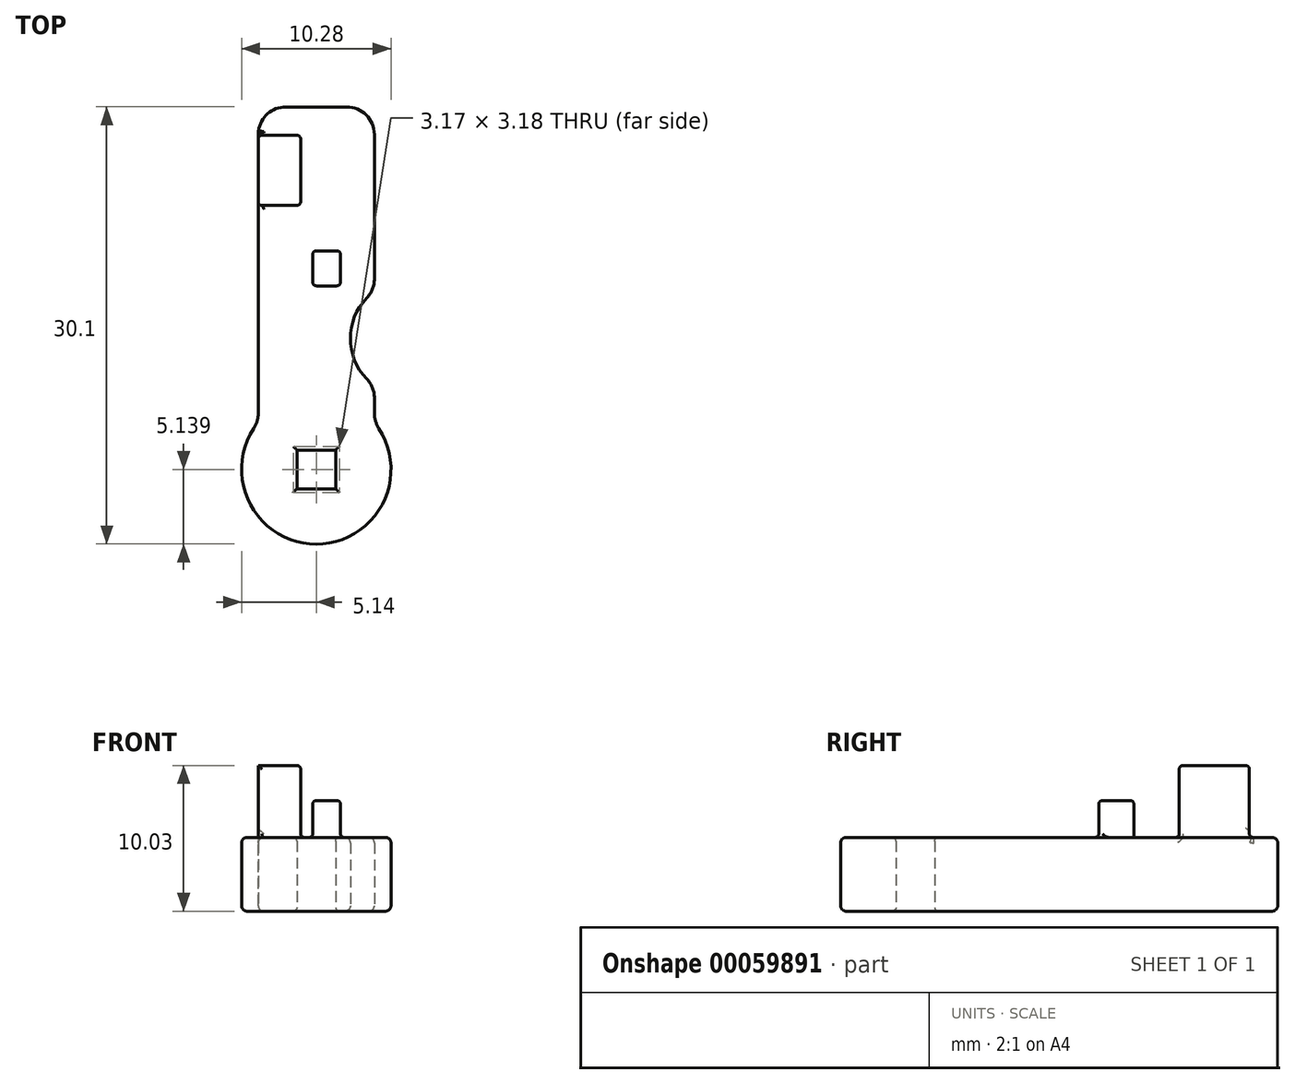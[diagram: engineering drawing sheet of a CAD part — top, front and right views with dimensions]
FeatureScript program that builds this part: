
annotation { "Feature Type Name" : "Feature", "Feature Type Description" : "" }
export const myFeature = defineFeature(function(context is Context, id is Id, definition is map)
    precondition{}
    {
        {
            var Q0;
            Q0=qCreatedBy(makeId("Top.planeOp"),FACE);
            var sketch = newSketch(context, id + "F0", { "sketchPlane" : qUnion([Q0])});
            skLineSegment(sketch, "E0.rect.bottom", {"start": v(4, 14.6) * mm, "end": v(-4, 14.6) * mm});
            skLineSegment(sketch, "E0.rect.left", {"start": v(4, 14.6) * mm, "end": v(4, 1.9) * mm});
            skLineSegment(sketch, "E0.rect.right", {"start": v(-4, 14.6) * mm, "end": v(-4, -7.12) * mm});
            skPoint(sketch, "E0.rect.middle", {"position": v(0, 0) * mm});
            skLineSegment(sketch, "E1.rect.bottom", {"start": v(1.33, -9.02) * mm, "end": v(-1.33, -9.02) * mm});
            skLineSegment(sketch, "E1.rect.top", {"start": v(1.33, -11.68) * mm, "end": v(-1.33, -11.68) * mm});
            skLineSegment(sketch, "E1.rect.left", {"start": v(1.33, -9.02) * mm, "end": v(1.33, -11.68) * mm});
            skLineSegment(sketch, "E1.rect.right", {"start": v(-1.33, -9.02) * mm, "end": v(-1.33, -11.68) * mm});
            skPoint(sketch, "E1.rect.middle", {"position": v(0, -10.35) * mm});
            skCircle(sketch, "E2", {"center": v(0, -10.35) * mm, "radius": 5.14 * mm});
            skArc(sketch, "E3", {"start": v(4, 1.9) * mm, "mid": v(2.35, -1.34) * mm, "end": v(4, -4.58) * mm});
            skLineSegment(sketch, "E4.trimOffspring", {"start": v(4, -4.58) * mm, "end": v(4, -7.12) * mm});
            skPoint(sketch, "E5.orphan", {"position": v(4, -14.6) * mm});
            skPoint(sketch, "E6.orphan", {"position": v(-4, -14.6) * mm});
            skLineSegment(sketch, "E7.rect.bottom", {"start": v(1.66, 2.29) * mm, "end": v(-0.24, 2.29) * mm});
            skLineSegment(sketch, "E7.rect.top", {"start": v(1.66, 4.7) * mm, "end": v(-0.24, 4.7) * mm});
            skLineSegment(sketch, "E7.rect.left", {"start": v(1.66, 2.29) * mm, "end": v(1.66, 4.7) * mm});
            skLineSegment(sketch, "E7.rect.right", {"start": v(-0.24, 2.29) * mm, "end": v(-0.24, 4.7) * mm});
            skPoint(sketch, "E7.rect.middle", {"position": v(0.71, 3.5) * mm});
            skLineSegment(sketch, "E8.bottom", {"start": v(-4, 12.65) * mm, "end": v(-1.08, 12.65) * mm});
            skLineSegment(sketch, "E8.top", {"start": v(-4, 7.82) * mm, "end": v(-1.08, 7.82) * mm});
            skLineSegment(sketch, "E8.left", {"start": v(-4, 12.65) * mm, "end": v(-4, 7.82) * mm});
            skLineSegment(sketch, "E8.right", {"start": v(-1.08, 12.65) * mm, "end": v(-1.08, 7.82) * mm});
            skSolve(sketch);
        }
        {
            var Q0;
            Q0 = qSketchRegion(id + "F0", true);
            var Q1;
            Q1=makeQuery(id+"F0.imprint","IMPRINT",FACE,{"disambiguationData":[TD([[makeQuery(id+"F0.imprint","IMPRINT",EDGE,{"derivedFrom":sQuery(id+"F0.wireOp",EDGE,"E7.rect.bottom")}),-1.0]])]});
            extrude(context, id + "F1", {"entities" : qUnion([Q0, Q1]), "depth" : 5.08 * mm});
        }
        {
            var Q0;
            Q0=makeQuery(id+"F0.imprint","IMPRINT",FACE,{"disambiguationData":[TD([[makeQuery(id+"F0.imprint","IMPRINT",EDGE,{"derivedFrom":sQuery(id+"F0.wireOp",EDGE,"E8.bottom")}),-1.0]])]});
            extrude(context, id + "F2", {"entities" : qUnion([Q0]), "operationType" : NewBodyOperationType.ADD, "depth" : 10.03 * mm});
        }
        {
            var Q0;
            Q0=makeQuery(id+"F0.imprint","IMPRINT",FACE,{"disambiguationData":[TD([[makeQuery(id+"F0.imprint","IMPRINT",EDGE,{"derivedFrom":sQuery(id+"F0.wireOp",EDGE,"E7.rect.bottom")}),-1.0]])]});
            extrude(context, id + "F3", {"entities" : qUnion([Q0]), "operationType" : NewBodyOperationType.ADD, "depth" : 7.62 * mm});
        }
        {
            var Q0;
            Q0=makeQuery(id+"F1.opExtrude","SWEPT_EDGE",EDGE,{"disambiguationData":[OSD([sQuery(id+"F0.wireOp",EDGE,"E0.rect.left"),sQuery(id+"F0.wireOp",EDGE,"E3")])]});
            var Q1;
            Q1=makeQuery(id+"F1.opExtrude","SWEPT_EDGE",EDGE,{"disambiguationData":[OSD([sQuery(id+"F0.wireOp",EDGE,"E3"),sQuery(id+"F0.wireOp",EDGE,"E4.trimOffspring")])]});
            var Q2;
            Q2=makeQuery(id+"F1.opExtrude","SWEPT_EDGE",EDGE,{"disambiguationData":[OSD([sQuery(id+"F0.wireOp",EDGE,"E2"),sQuery(id+"F0.wireOp",EDGE,"E4.trimOffspring")])]});
            var Q3;
            Q3=makeQuery(id+"F1.opExtrude","SWEPT_EDGE",EDGE,{"disambiguationData":[OSD([sQuery(id+"F0.wireOp",EDGE,"E0.rect.right"),sQuery(id+"F0.wireOp",EDGE,"E2")])]});
            var Q4;
            Q4=makeQuery(id+"F1.opExtrude","SWEPT_EDGE",EDGE,{"disambiguationData":[OSD([sQuery(id+"F0.wireOp",EDGE,"E0.rect.bottom"),sQuery(id+"F0.wireOp",EDGE,"E0.rect.right")])]});
            var Q5;
            Q5=makeQuery(id+"F1.opExtrude","SWEPT_EDGE",EDGE,{"disambiguationData":[OSD([sQuery(id+"F0.wireOp",EDGE,"E0.rect.bottom"),sQuery(id+"F0.wireOp",EDGE,"E0.rect.left")])]});
            fillet(context, id + "F4", {"entities" : qUnion([Q0, Q1, Q2, Q3, Q4, Q5]), "radius" : 1.9 * mm, "tangentPropagation" : true, "allowEdgeOverflow" : false});
        }
        {
            var Q0;
            Q0=makeQuery(id+"F2.opExtrude","CAP_EDGE",EDGE,{"disambiguationData":[OSD([sQuery(id+"F0.wireOp",EDGE,"E8.right")])],"isStart":false});
            var Q1;
            Q1=makeQuery(id+"F2.opExtrude","CAP_EDGE",EDGE,{"disambiguationData":[OSD([sQuery(id+"F0.wireOp",EDGE,"E8.top")])],"isStart":false});
            var Q2;
            Q2=makeQuery(id+"F2.opExtrude","CAP_EDGE",EDGE,{"disambiguationData":[OSD([sQuery(id+"F0.wireOp",EDGE,"E8.left")])],"isStart":false});
            var Q3;
            Q3=makeQuery(id+"F2.opExtrude","CAP_EDGE",EDGE,{"disambiguationData":[OSD([sQuery(id+"F0.wireOp",EDGE,"E8.bottom")])],"isStart":false});
            var Q4;
            Q4=makeQuery(id+"F2.opExtrude","SWEPT_EDGE",EDGE,{"disambiguationData":[OSD([sQuery(id+"F0.wireOp",EDGE,"E8.top"),sQuery(id+"F0.wireOp",EDGE,"E8.right")])]});
            var Q5;
            Q5=makeQuery(id+"F2.opExtrude","SWEPT_EDGE",EDGE,{"disambiguationData":[OSD([sQuery(id+"F0.wireOp",EDGE,"E0.rect.right"),sQuery(id+"F0.wireOp",EDGE,"E8.top"),sQuery(id+"F0.wireOp",EDGE,"E8.left")])]});
            var Q6;
            Q6=makeQuery(id+"F2.opExtrude","SWEPT_EDGE",EDGE,{"disambiguationData":[OSD([sQuery(id+"F0.wireOp",EDGE,"E8.bottom"),sQuery(id+"F0.wireOp",EDGE,"E8.right")])]});
            var Q7;
            Q7=makeQuery(id+"F2.opExtrude","SWEPT_EDGE",EDGE,{"disambiguationData":[OSD([sQuery(id+"F0.wireOp",EDGE,"E0.rect.right"),sQuery(id+"F0.wireOp",EDGE,"E8.bottom"),sQuery(id+"F0.wireOp",EDGE,"E8.left")])]});
            var Q8;
            Q8=makeQuery(id+"F3.opExtrude","SWEPT_EDGE",EDGE,{"disambiguationData":[OSD([sQuery(id+"F0.wireOp",EDGE,"E7.rect.bottom"),sQuery(id+"F0.wireOp",EDGE,"E7.rect.right")])]});
            var Q9;
            Q9=makeQuery(id+"F3.opExtrude","CAP_EDGE",EDGE,{"disambiguationData":[OSD([sQuery(id+"F0.wireOp",EDGE,"E7.rect.right")])],"isStart":false});
            var Q10;
            Q10=makeQuery(id+"F3.opExtrude","CAP_EDGE",EDGE,{"disambiguationData":[OSD([sQuery(id+"F0.wireOp",EDGE,"E7.rect.bottom")])],"isStart":false});
            var Q11;
            Q11=makeQuery(id+"F3.opExtrude","SWEPT_EDGE",EDGE,{"disambiguationData":[OSD([sQuery(id+"F0.wireOp",EDGE,"E7.rect.bottom"),sQuery(id+"F0.wireOp",EDGE,"E7.rect.left")])]});
            var Q12;
            Q12=makeQuery(id+"F3.opExtrude","CAP_EDGE",EDGE,{"disambiguationData":[OSD([sQuery(id+"F0.wireOp",EDGE,"E7.rect.left")])],"isStart":false});
            var Q13;
            Q13=makeQuery(id+"F3.opExtrude","CAP_EDGE",EDGE,{"disambiguationData":[OSD([sQuery(id+"F0.wireOp",EDGE,"E7.rect.top")])],"isStart":false});
            var Q14;
            Q14=makeQuery(id+"F3.opExtrude","SWEPT_EDGE",EDGE,{"disambiguationData":[OSD([sQuery(id+"F0.wireOp",EDGE,"E7.rect.top"),sQuery(id+"F0.wireOp",EDGE,"E7.rect.left")])]});
            var Q15;
            Q15=makeQuery(id+"F3.opExtrude","SWEPT_EDGE",EDGE,{"disambiguationData":[OSD([sQuery(id+"F0.wireOp",EDGE,"E7.rect.top"),sQuery(id+"F0.wireOp",EDGE,"E7.rect.right")])]});
            var Q16;
            Q16=makeQuery(id+"F3.boolean.opBoolean","INTERSECT",EDGE,{"derivedFrom":[makeQuery(id+"F1.opExtrude","CAP_FACE",FACE,{"disambiguationData":[OSD([sQuery(id+"F0.wireOp",EDGE,"E0.rect.bottom"),sQuery(id+"F0.wireOp",EDGE,"E0.rect.left"),sQuery(id+"F0.wireOp",EDGE,"E0.rect.right"),sQuery(id+"F0.wireOp",EDGE,"E1.rect.bottom"),sQuery(id+"F0.wireOp",EDGE,"E1.rect.top"),sQuery(id+"F0.wireOp",EDGE,"E1.rect.left"),sQuery(id+"F0.wireOp",EDGE,"E1.rect.right"),sQuery(id+"F0.wireOp",EDGE,"E2"),sQuery(id+"F0.wireOp",EDGE,"E3"),sQuery(id+"F0.wireOp",EDGE,"E4.trimOffspring"),sQuery(id+"F0.wireOp",EDGE,"E8.left")])],"isStart":false}),makeQuery(id+"F3.opExtrude","SWEPT_FACE",FACE,{"disambiguationData":[OSD([sQuery(id+"F0.wireOp",EDGE,"E7.rect.bottom")])]})]});
            fillet(context, id + "F5", {"entities" : qUnion([Q0, Q1, Q2, Q3, Q4, Q5, Q6, Q7, Q8, Q9, Q10, Q11, Q12, Q13, Q14, Q15, Q16]), "radius" : 0.25 * mm, "tangentPropagation" : true, "allowEdgeOverflow" : false});
        }
        {
            var Q0;
            Q0=makeQuery(id+"F2.boolean.opBoolean","INTERSECT",EDGE,{"derivedFrom":[makeQuery(id+"F1.opExtrude","CAP_FACE",FACE,{"disambiguationData":[OSD([sQuery(id+"F0.wireOp",EDGE,"E0.rect.bottom"),sQuery(id+"F0.wireOp",EDGE,"E0.rect.left"),sQuery(id+"F0.wireOp",EDGE,"E0.rect.right"),sQuery(id+"F0.wireOp",EDGE,"E1.rect.bottom"),sQuery(id+"F0.wireOp",EDGE,"E1.rect.top"),sQuery(id+"F0.wireOp",EDGE,"E1.rect.left"),sQuery(id+"F0.wireOp",EDGE,"E1.rect.right"),sQuery(id+"F0.wireOp",EDGE,"E2"),sQuery(id+"F0.wireOp",EDGE,"E3"),sQuery(id+"F0.wireOp",EDGE,"E4.trimOffspring"),sQuery(id+"F0.wireOp",EDGE,"E8.left")])],"isStart":false}),makeQuery(id+"F2.opExtrude","SWEPT_FACE",FACE,{"disambiguationData":[OSD([sQuery(id+"F0.wireOp",EDGE,"E8.top")])]})]});
            var Q1;
            Q1=makeQuery(id+"F5.opFillet","BLEND_EDGE",EDGE,{"blendedFrom":[makeQuery(id+"F2.opExtrude","SWEPT_EDGE",EDGE,{"disambiguationData":[OSD([sQuery(id+"F0.wireOp",EDGE,"E8.top"),sQuery(id+"F0.wireOp",EDGE,"E8.right")])]}),makeQuery(id+"F1.opExtrude","CAP_FACE",FACE,{"disambiguationData":[OSD([sQuery(id+"F0.wireOp",EDGE,"E0.rect.bottom"),sQuery(id+"F0.wireOp",EDGE,"E0.rect.left"),sQuery(id+"F0.wireOp",EDGE,"E0.rect.right"),sQuery(id+"F0.wireOp",EDGE,"E1.rect.bottom"),sQuery(id+"F0.wireOp",EDGE,"E1.rect.top"),sQuery(id+"F0.wireOp",EDGE,"E1.rect.left"),sQuery(id+"F0.wireOp",EDGE,"E1.rect.right"),sQuery(id+"F0.wireOp",EDGE,"E2"),sQuery(id+"F0.wireOp",EDGE,"E3"),sQuery(id+"F0.wireOp",EDGE,"E4.trimOffspring"),sQuery(id+"F0.wireOp",EDGE,"E8.left")])],"isStart":false})],"blendedInto":[makeQuery(id+"F1.opExtrude","CAP_FACE",FACE,{"disambiguationData":[OSD([sQuery(id+"F0.wireOp",EDGE,"E0.rect.bottom"),sQuery(id+"F0.wireOp",EDGE,"E0.rect.left"),sQuery(id+"F0.wireOp",EDGE,"E0.rect.right"),sQuery(id+"F0.wireOp",EDGE,"E1.rect.bottom"),sQuery(id+"F0.wireOp",EDGE,"E1.rect.top"),sQuery(id+"F0.wireOp",EDGE,"E1.rect.left"),sQuery(id+"F0.wireOp",EDGE,"E1.rect.right"),sQuery(id+"F0.wireOp",EDGE,"E2"),sQuery(id+"F0.wireOp",EDGE,"E3"),sQuery(id+"F0.wireOp",EDGE,"E4.trimOffspring"),sQuery(id+"F0.wireOp",EDGE,"E8.left")])],"isStart":false})]});
            var Q2;
            {var subQ0=sQuery(id+"F0.wireOp",EDGE,"E8.left");var subQ1=sQuery(id+"F0.wireOp",EDGE,"E0.rect.right");Q2=makeQuery(id+"F5.opFillet","BLEND_EDGE",EDGE,{"blendedFrom":[makeQuery(id+"F2.opExtrude","SWEPT_EDGE",EDGE,{"disambiguationData":[OSD([subQ1,sQuery(id+"F0.wireOp",EDGE,"E8.top"),subQ0])]}),makeQuery(id+"F1.opExtrude","CAP_FACE",FACE,{"disambiguationData":[OSD([sQuery(id+"F0.wireOp",EDGE,"E0.rect.bottom"),sQuery(id+"F0.wireOp",EDGE,"E0.rect.left"),subQ1,sQuery(id+"F0.wireOp",EDGE,"E1.rect.bottom"),sQuery(id+"F0.wireOp",EDGE,"E1.rect.top"),sQuery(id+"F0.wireOp",EDGE,"E1.rect.left"),sQuery(id+"F0.wireOp",EDGE,"E1.rect.right"),sQuery(id+"F0.wireOp",EDGE,"E2"),sQuery(id+"F0.wireOp",EDGE,"E3"),sQuery(id+"F0.wireOp",EDGE,"E4.trimOffspring"),subQ0])],"isStart":false})],"blendedInto":[makeQuery(id+"F1.opExtrude","CAP_FACE",FACE,{"disambiguationData":[OSD([sQuery(id+"F0.wireOp",EDGE,"E0.rect.bottom"),sQuery(id+"F0.wireOp",EDGE,"E0.rect.left"),subQ1,sQuery(id+"F0.wireOp",EDGE,"E1.rect.bottom"),sQuery(id+"F0.wireOp",EDGE,"E1.rect.top"),sQuery(id+"F0.wireOp",EDGE,"E1.rect.left"),sQuery(id+"F0.wireOp",EDGE,"E1.rect.right"),sQuery(id+"F0.wireOp",EDGE,"E2"),sQuery(id+"F0.wireOp",EDGE,"E3"),sQuery(id+"F0.wireOp",EDGE,"E4.trimOffspring"),subQ0])],"isStart":false})]});}
            var Q3;
            Q3=makeQuery(id+"F2.boolean.opBoolean","INTERSECT",EDGE,{"derivedFrom":[makeQuery(id+"F1.opExtrude","CAP_FACE",FACE,{"disambiguationData":[OSD([sQuery(id+"F0.wireOp",EDGE,"E0.rect.bottom"),sQuery(id+"F0.wireOp",EDGE,"E0.rect.left"),sQuery(id+"F0.wireOp",EDGE,"E0.rect.right"),sQuery(id+"F0.wireOp",EDGE,"E1.rect.bottom"),sQuery(id+"F0.wireOp",EDGE,"E1.rect.top"),sQuery(id+"F0.wireOp",EDGE,"E1.rect.left"),sQuery(id+"F0.wireOp",EDGE,"E1.rect.right"),sQuery(id+"F0.wireOp",EDGE,"E2"),sQuery(id+"F0.wireOp",EDGE,"E3"),sQuery(id+"F0.wireOp",EDGE,"E4.trimOffspring"),sQuery(id+"F0.wireOp",EDGE,"E8.left")])],"isStart":false}),makeQuery(id+"F2.opExtrude","SWEPT_FACE",FACE,{"disambiguationData":[OSD([sQuery(id+"F0.wireOp",EDGE,"E8.right")])]})]});
            var Q4;
            Q4=makeQuery(id+"F5.opFillet","BLEND_EDGE",EDGE,{"blendedFrom":[makeQuery(id+"F2.opExtrude","SWEPT_EDGE",EDGE,{"disambiguationData":[OSD([sQuery(id+"F0.wireOp",EDGE,"E8.bottom"),sQuery(id+"F0.wireOp",EDGE,"E8.right")])]}),makeQuery(id+"F1.opExtrude","CAP_FACE",FACE,{"disambiguationData":[OSD([sQuery(id+"F0.wireOp",EDGE,"E0.rect.bottom"),sQuery(id+"F0.wireOp",EDGE,"E0.rect.left"),sQuery(id+"F0.wireOp",EDGE,"E0.rect.right"),sQuery(id+"F0.wireOp",EDGE,"E1.rect.bottom"),sQuery(id+"F0.wireOp",EDGE,"E1.rect.top"),sQuery(id+"F0.wireOp",EDGE,"E1.rect.left"),sQuery(id+"F0.wireOp",EDGE,"E1.rect.right"),sQuery(id+"F0.wireOp",EDGE,"E2"),sQuery(id+"F0.wireOp",EDGE,"E3"),sQuery(id+"F0.wireOp",EDGE,"E4.trimOffspring"),sQuery(id+"F0.wireOp",EDGE,"E8.left")])],"isStart":false})],"blendedInto":[makeQuery(id+"F1.opExtrude","CAP_FACE",FACE,{"disambiguationData":[OSD([sQuery(id+"F0.wireOp",EDGE,"E0.rect.bottom"),sQuery(id+"F0.wireOp",EDGE,"E0.rect.left"),sQuery(id+"F0.wireOp",EDGE,"E0.rect.right"),sQuery(id+"F0.wireOp",EDGE,"E1.rect.bottom"),sQuery(id+"F0.wireOp",EDGE,"E1.rect.top"),sQuery(id+"F0.wireOp",EDGE,"E1.rect.left"),sQuery(id+"F0.wireOp",EDGE,"E1.rect.right"),sQuery(id+"F0.wireOp",EDGE,"E2"),sQuery(id+"F0.wireOp",EDGE,"E3"),sQuery(id+"F0.wireOp",EDGE,"E4.trimOffspring"),sQuery(id+"F0.wireOp",EDGE,"E8.left")])],"isStart":false})]});
            var Q5;
            Q5=makeQuery(id+"F2.boolean.opBoolean","INTERSECT",EDGE,{"derivedFrom":[makeQuery(id+"F1.opExtrude","CAP_FACE",FACE,{"disambiguationData":[OSD([sQuery(id+"F0.wireOp",EDGE,"E0.rect.bottom"),sQuery(id+"F0.wireOp",EDGE,"E0.rect.left"),sQuery(id+"F0.wireOp",EDGE,"E0.rect.right"),sQuery(id+"F0.wireOp",EDGE,"E1.rect.bottom"),sQuery(id+"F0.wireOp",EDGE,"E1.rect.top"),sQuery(id+"F0.wireOp",EDGE,"E1.rect.left"),sQuery(id+"F0.wireOp",EDGE,"E1.rect.right"),sQuery(id+"F0.wireOp",EDGE,"E2"),sQuery(id+"F0.wireOp",EDGE,"E3"),sQuery(id+"F0.wireOp",EDGE,"E4.trimOffspring"),sQuery(id+"F0.wireOp",EDGE,"E8.left")])],"isStart":false}),makeQuery(id+"F2.opExtrude","SWEPT_FACE",FACE,{"disambiguationData":[OSD([sQuery(id+"F0.wireOp",EDGE,"E8.bottom")])]})]});
            var Q6;
            {var subQ0=sQuery(id+"F0.wireOp",EDGE,"E8.left");var subQ1=sQuery(id+"F0.wireOp",EDGE,"E0.rect.right");Q6=makeQuery(id+"F5.opFillet","BLEND_EDGE",EDGE,{"blendedFrom":[makeQuery(id+"F2.opExtrude","SWEPT_EDGE",EDGE,{"disambiguationData":[OSD([subQ1,sQuery(id+"F0.wireOp",EDGE,"E8.bottom"),subQ0])]}),makeQuery(id+"F1.opExtrude","CAP_FACE",FACE,{"disambiguationData":[OSD([sQuery(id+"F0.wireOp",EDGE,"E0.rect.bottom"),sQuery(id+"F0.wireOp",EDGE,"E0.rect.left"),subQ1,sQuery(id+"F0.wireOp",EDGE,"E1.rect.bottom"),sQuery(id+"F0.wireOp",EDGE,"E1.rect.top"),sQuery(id+"F0.wireOp",EDGE,"E1.rect.left"),sQuery(id+"F0.wireOp",EDGE,"E1.rect.right"),sQuery(id+"F0.wireOp",EDGE,"E2"),sQuery(id+"F0.wireOp",EDGE,"E3"),sQuery(id+"F0.wireOp",EDGE,"E4.trimOffspring"),subQ0])],"isStart":false})],"blendedInto":[makeQuery(id+"F1.opExtrude","CAP_FACE",FACE,{"disambiguationData":[OSD([sQuery(id+"F0.wireOp",EDGE,"E0.rect.bottom"),sQuery(id+"F0.wireOp",EDGE,"E0.rect.left"),subQ1,sQuery(id+"F0.wireOp",EDGE,"E1.rect.bottom"),sQuery(id+"F0.wireOp",EDGE,"E1.rect.top"),sQuery(id+"F0.wireOp",EDGE,"E1.rect.left"),sQuery(id+"F0.wireOp",EDGE,"E1.rect.right"),sQuery(id+"F0.wireOp",EDGE,"E2"),sQuery(id+"F0.wireOp",EDGE,"E3"),sQuery(id+"F0.wireOp",EDGE,"E4.trimOffspring"),subQ0])],"isStart":false})]});}
            fillet(context, id + "F6", {"entities" : qUnion([Q0, Q1, Q2, Q3, Q4, Q5, Q6]), "radius" : 0.25 * mm, "allowEdgeOverflow" : false});
        }
        {
            var Q0;
            {var subQ0=sQuery(id+"F0.wireOp",EDGE,"E8.left");var subQ1=sQuery(id+"F0.wireOp",EDGE,"E0.rect.right");var subQ2=sQuery(id+"F0.wireOp",EDGE,"E2");Q0=makeQuery(id+"F2.boolean.opBoolean","SPLIT",EDGE,{"disambiguationData":[TD([makeQuery(id+"F1.opExtrude","SWEPT_FACE",FACE,{"disambiguationData":[OSD([subQ2])]})])],"derivedFrom":makeQuery(id+"F1.opExtrude","CAP_EDGE",EDGE,{"disambiguationData":[OSD([subQ1,subQ0])],"isStart":false})});}
            var Q1;
            {var subQ0=sQuery(id+"F0.wireOp",EDGE,"E2");var subQ1=sQuery(id+"F0.wireOp",EDGE,"E0.rect.right");Q1=makeQuery(id+"F4.opFillet","BLEND_EDGE",EDGE,{"blendedFrom":[makeQuery(id+"F1.opExtrude","SWEPT_EDGE",EDGE,{"disambiguationData":[OSD([subQ1,subQ0])]}),makeQuery(id+"F1.opExtrude","CAP_FACE",FACE,{"disambiguationData":[OSD([sQuery(id+"F0.wireOp",EDGE,"E0.rect.bottom"),sQuery(id+"F0.wireOp",EDGE,"E0.rect.left"),subQ1,sQuery(id+"F0.wireOp",EDGE,"E1.rect.bottom"),sQuery(id+"F0.wireOp",EDGE,"E1.rect.top"),sQuery(id+"F0.wireOp",EDGE,"E1.rect.left"),sQuery(id+"F0.wireOp",EDGE,"E1.rect.right"),subQ0,sQuery(id+"F0.wireOp",EDGE,"E3"),sQuery(id+"F0.wireOp",EDGE,"E4.trimOffspring"),sQuery(id+"F0.wireOp",EDGE,"E8.left")])],"isStart":false})],"blendedInto":[makeQuery(id+"F1.opExtrude","CAP_FACE",FACE,{"disambiguationData":[OSD([sQuery(id+"F0.wireOp",EDGE,"E0.rect.bottom"),sQuery(id+"F0.wireOp",EDGE,"E0.rect.left"),subQ1,sQuery(id+"F0.wireOp",EDGE,"E1.rect.bottom"),sQuery(id+"F0.wireOp",EDGE,"E1.rect.top"),sQuery(id+"F0.wireOp",EDGE,"E1.rect.left"),sQuery(id+"F0.wireOp",EDGE,"E1.rect.right"),subQ0,sQuery(id+"F0.wireOp",EDGE,"E3"),sQuery(id+"F0.wireOp",EDGE,"E4.trimOffspring"),sQuery(id+"F0.wireOp",EDGE,"E8.left")])],"isStart":false})]});}
            var Q2;
            Q2=makeQuery(id+"F1.opExtrude","CAP_EDGE",EDGE,{"disambiguationData":[OSD([sQuery(id+"F0.wireOp",EDGE,"E2")])],"isStart":false});
            var Q3;
            {var subQ0=sQuery(id+"F0.wireOp",EDGE,"E4.trimOffspring");var subQ1=sQuery(id+"F0.wireOp",EDGE,"E2");Q3=makeQuery(id+"F4.opFillet","BLEND_EDGE",EDGE,{"blendedFrom":[makeQuery(id+"F1.opExtrude","SWEPT_EDGE",EDGE,{"disambiguationData":[OSD([subQ1,subQ0])]}),makeQuery(id+"F1.opExtrude","CAP_FACE",FACE,{"disambiguationData":[OSD([sQuery(id+"F0.wireOp",EDGE,"E0.rect.bottom"),sQuery(id+"F0.wireOp",EDGE,"E0.rect.left"),sQuery(id+"F0.wireOp",EDGE,"E0.rect.right"),sQuery(id+"F0.wireOp",EDGE,"E1.rect.bottom"),sQuery(id+"F0.wireOp",EDGE,"E1.rect.top"),sQuery(id+"F0.wireOp",EDGE,"E1.rect.left"),sQuery(id+"F0.wireOp",EDGE,"E1.rect.right"),subQ1,sQuery(id+"F0.wireOp",EDGE,"E3"),subQ0,sQuery(id+"F0.wireOp",EDGE,"E8.left")])],"isStart":false})],"blendedInto":[makeQuery(id+"F1.opExtrude","CAP_FACE",FACE,{"disambiguationData":[OSD([sQuery(id+"F0.wireOp",EDGE,"E0.rect.bottom"),sQuery(id+"F0.wireOp",EDGE,"E0.rect.left"),sQuery(id+"F0.wireOp",EDGE,"E0.rect.right"),sQuery(id+"F0.wireOp",EDGE,"E1.rect.bottom"),sQuery(id+"F0.wireOp",EDGE,"E1.rect.top"),sQuery(id+"F0.wireOp",EDGE,"E1.rect.left"),sQuery(id+"F0.wireOp",EDGE,"E1.rect.right"),subQ1,sQuery(id+"F0.wireOp",EDGE,"E3"),subQ0,sQuery(id+"F0.wireOp",EDGE,"E8.left")])],"isStart":false})]});}
            var Q4;
            Q4=makeQuery(id+"F1.opExtrude","CAP_EDGE",EDGE,{"disambiguationData":[OSD([sQuery(id+"F0.wireOp",EDGE,"E4.trimOffspring")])],"isStart":false});
            var Q5;
            Q5=makeQuery(id+"F1.opExtrude","CAP_EDGE",EDGE,{"disambiguationData":[OSD([sQuery(id+"F0.wireOp",EDGE,"E3")])],"isStart":false});
            var Q6;
            {var subQ0=sQuery(id+"F0.wireOp",EDGE,"E3");var subQ1=sQuery(id+"F0.wireOp",EDGE,"E0.rect.left");Q6=makeQuery(id+"F4.opFillet","BLEND_EDGE",EDGE,{"blendedFrom":[makeQuery(id+"F1.opExtrude","SWEPT_EDGE",EDGE,{"disambiguationData":[OSD([subQ1,subQ0])]}),makeQuery(id+"F1.opExtrude","CAP_FACE",FACE,{"disambiguationData":[OSD([sQuery(id+"F0.wireOp",EDGE,"E0.rect.bottom"),subQ1,sQuery(id+"F0.wireOp",EDGE,"E0.rect.right"),sQuery(id+"F0.wireOp",EDGE,"E1.rect.bottom"),sQuery(id+"F0.wireOp",EDGE,"E1.rect.top"),sQuery(id+"F0.wireOp",EDGE,"E1.rect.left"),sQuery(id+"F0.wireOp",EDGE,"E1.rect.right"),sQuery(id+"F0.wireOp",EDGE,"E2"),subQ0,sQuery(id+"F0.wireOp",EDGE,"E4.trimOffspring"),sQuery(id+"F0.wireOp",EDGE,"E8.left")])],"isStart":false})],"blendedInto":[makeQuery(id+"F1.opExtrude","CAP_FACE",FACE,{"disambiguationData":[OSD([sQuery(id+"F0.wireOp",EDGE,"E0.rect.bottom"),subQ1,sQuery(id+"F0.wireOp",EDGE,"E0.rect.right"),sQuery(id+"F0.wireOp",EDGE,"E1.rect.bottom"),sQuery(id+"F0.wireOp",EDGE,"E1.rect.top"),sQuery(id+"F0.wireOp",EDGE,"E1.rect.left"),sQuery(id+"F0.wireOp",EDGE,"E1.rect.right"),sQuery(id+"F0.wireOp",EDGE,"E2"),subQ0,sQuery(id+"F0.wireOp",EDGE,"E4.trimOffspring"),sQuery(id+"F0.wireOp",EDGE,"E8.left")])],"isStart":false})]});}
            var Q7;
            {var subQ0=sQuery(id+"F0.wireOp",EDGE,"E4.trimOffspring");var subQ1=sQuery(id+"F0.wireOp",EDGE,"E3");Q7=makeQuery(id+"F4.opFillet","BLEND_EDGE",EDGE,{"blendedFrom":[makeQuery(id+"F1.opExtrude","SWEPT_EDGE",EDGE,{"disambiguationData":[OSD([subQ1,subQ0])]}),makeQuery(id+"F1.opExtrude","CAP_FACE",FACE,{"disambiguationData":[OSD([sQuery(id+"F0.wireOp",EDGE,"E0.rect.bottom"),sQuery(id+"F0.wireOp",EDGE,"E0.rect.left"),sQuery(id+"F0.wireOp",EDGE,"E0.rect.right"),sQuery(id+"F0.wireOp",EDGE,"E1.rect.bottom"),sQuery(id+"F0.wireOp",EDGE,"E1.rect.top"),sQuery(id+"F0.wireOp",EDGE,"E1.rect.left"),sQuery(id+"F0.wireOp",EDGE,"E1.rect.right"),sQuery(id+"F0.wireOp",EDGE,"E2"),subQ1,subQ0,sQuery(id+"F0.wireOp",EDGE,"E8.left")])],"isStart":false})],"blendedInto":[makeQuery(id+"F1.opExtrude","CAP_FACE",FACE,{"disambiguationData":[OSD([sQuery(id+"F0.wireOp",EDGE,"E0.rect.bottom"),sQuery(id+"F0.wireOp",EDGE,"E0.rect.left"),sQuery(id+"F0.wireOp",EDGE,"E0.rect.right"),sQuery(id+"F0.wireOp",EDGE,"E1.rect.bottom"),sQuery(id+"F0.wireOp",EDGE,"E1.rect.top"),sQuery(id+"F0.wireOp",EDGE,"E1.rect.left"),sQuery(id+"F0.wireOp",EDGE,"E1.rect.right"),sQuery(id+"F0.wireOp",EDGE,"E2"),subQ1,subQ0,sQuery(id+"F0.wireOp",EDGE,"E8.left")])],"isStart":false})]});}
            var Q8;
            Q8=makeQuery(id+"F1.opExtrude","CAP_EDGE",EDGE,{"disambiguationData":[OSD([sQuery(id+"F0.wireOp",EDGE,"E0.rect.left")])],"isStart":false});
            var Q9;
            {var subQ0=sQuery(id+"F0.wireOp",EDGE,"E0.rect.left");var subQ1=sQuery(id+"F0.wireOp",EDGE,"E0.rect.bottom");Q9=makeQuery(id+"F4.opFillet","BLEND_EDGE",EDGE,{"blendedFrom":[makeQuery(id+"F1.opExtrude","SWEPT_EDGE",EDGE,{"disambiguationData":[OSD([subQ1,subQ0])]}),makeQuery(id+"F1.opExtrude","CAP_FACE",FACE,{"disambiguationData":[OSD([subQ1,subQ0,sQuery(id+"F0.wireOp",EDGE,"E0.rect.right"),sQuery(id+"F0.wireOp",EDGE,"E1.rect.bottom"),sQuery(id+"F0.wireOp",EDGE,"E1.rect.top"),sQuery(id+"F0.wireOp",EDGE,"E1.rect.left"),sQuery(id+"F0.wireOp",EDGE,"E1.rect.right"),sQuery(id+"F0.wireOp",EDGE,"E2"),sQuery(id+"F0.wireOp",EDGE,"E3"),sQuery(id+"F0.wireOp",EDGE,"E4.trimOffspring"),sQuery(id+"F0.wireOp",EDGE,"E8.left")])],"isStart":false})],"blendedInto":[makeQuery(id+"F1.opExtrude","CAP_FACE",FACE,{"disambiguationData":[OSD([subQ1,subQ0,sQuery(id+"F0.wireOp",EDGE,"E0.rect.right"),sQuery(id+"F0.wireOp",EDGE,"E1.rect.bottom"),sQuery(id+"F0.wireOp",EDGE,"E1.rect.top"),sQuery(id+"F0.wireOp",EDGE,"E1.rect.left"),sQuery(id+"F0.wireOp",EDGE,"E1.rect.right"),sQuery(id+"F0.wireOp",EDGE,"E2"),sQuery(id+"F0.wireOp",EDGE,"E3"),sQuery(id+"F0.wireOp",EDGE,"E4.trimOffspring"),sQuery(id+"F0.wireOp",EDGE,"E8.left")])],"isStart":false})]});}
            var Q10;
            Q10=makeQuery(id+"F1.opExtrude","CAP_EDGE",EDGE,{"disambiguationData":[OSD([sQuery(id+"F0.wireOp",EDGE,"E0.rect.bottom")])],"isStart":false});
            var Q11;
            {var subQ0=sQuery(id+"F0.wireOp",EDGE,"E0.rect.right");var subQ1=sQuery(id+"F0.wireOp",EDGE,"E0.rect.bottom");Q11=makeQuery(id+"F4.opFillet","BLEND_EDGE",EDGE,{"blendedFrom":[makeQuery(id+"F1.opExtrude","SWEPT_EDGE",EDGE,{"disambiguationData":[OSD([subQ1,subQ0])]}),makeQuery(id+"F1.opExtrude","CAP_FACE",FACE,{"disambiguationData":[OSD([subQ1,sQuery(id+"F0.wireOp",EDGE,"E0.rect.left"),subQ0,sQuery(id+"F0.wireOp",EDGE,"E1.rect.bottom"),sQuery(id+"F0.wireOp",EDGE,"E1.rect.top"),sQuery(id+"F0.wireOp",EDGE,"E1.rect.left"),sQuery(id+"F0.wireOp",EDGE,"E1.rect.right"),sQuery(id+"F0.wireOp",EDGE,"E2"),sQuery(id+"F0.wireOp",EDGE,"E3"),sQuery(id+"F0.wireOp",EDGE,"E4.trimOffspring"),sQuery(id+"F0.wireOp",EDGE,"E8.left")])],"isStart":false})],"blendedInto":[makeQuery(id+"F1.opExtrude","CAP_FACE",FACE,{"disambiguationData":[OSD([subQ1,sQuery(id+"F0.wireOp",EDGE,"E0.rect.left"),subQ0,sQuery(id+"F0.wireOp",EDGE,"E1.rect.bottom"),sQuery(id+"F0.wireOp",EDGE,"E1.rect.top"),sQuery(id+"F0.wireOp",EDGE,"E1.rect.left"),sQuery(id+"F0.wireOp",EDGE,"E1.rect.right"),sQuery(id+"F0.wireOp",EDGE,"E2"),sQuery(id+"F0.wireOp",EDGE,"E3"),sQuery(id+"F0.wireOp",EDGE,"E4.trimOffspring"),sQuery(id+"F0.wireOp",EDGE,"E8.left")])],"isStart":false})]});}
            var Q12;
            {var subQ0=sQuery(id+"F0.wireOp",EDGE,"E8.left");var subQ1=sQuery(id+"F0.wireOp",EDGE,"E0.rect.right");Q12=makeQuery(id+"F6.opFillet","BLEND_EDGE",EDGE,{"blendedFrom":[makeQuery(id+"F5.opFillet","BLEND_EDGE",EDGE,{"blendedFrom":[makeQuery(id+"F2.opExtrude","SWEPT_EDGE",EDGE,{"disambiguationData":[OSD([subQ1,sQuery(id+"F0.wireOp",EDGE,"E8.top"),subQ0])]}),makeQuery(id+"F1.opExtrude","CAP_FACE",FACE,{"disambiguationData":[OSD([sQuery(id+"F0.wireOp",EDGE,"E0.rect.bottom"),sQuery(id+"F0.wireOp",EDGE,"E0.rect.left"),subQ1,sQuery(id+"F0.wireOp",EDGE,"E1.rect.bottom"),sQuery(id+"F0.wireOp",EDGE,"E1.rect.top"),sQuery(id+"F0.wireOp",EDGE,"E1.rect.left"),sQuery(id+"F0.wireOp",EDGE,"E1.rect.right"),sQuery(id+"F0.wireOp",EDGE,"E2"),sQuery(id+"F0.wireOp",EDGE,"E3"),sQuery(id+"F0.wireOp",EDGE,"E4.trimOffspring"),subQ0])],"isStart":false})],"blendedInto":[makeQuery(id+"F1.opExtrude","CAP_FACE",FACE,{"disambiguationData":[OSD([sQuery(id+"F0.wireOp",EDGE,"E0.rect.bottom"),sQuery(id+"F0.wireOp",EDGE,"E0.rect.left"),subQ1,sQuery(id+"F0.wireOp",EDGE,"E1.rect.bottom"),sQuery(id+"F0.wireOp",EDGE,"E1.rect.top"),sQuery(id+"F0.wireOp",EDGE,"E1.rect.left"),sQuery(id+"F0.wireOp",EDGE,"E1.rect.right"),sQuery(id+"F0.wireOp",EDGE,"E2"),sQuery(id+"F0.wireOp",EDGE,"E3"),sQuery(id+"F0.wireOp",EDGE,"E4.trimOffspring"),subQ0])],"isStart":false})]}),makeQuery(id+"F2.boolean.opBoolean","MERGE",FACE,{"derivedFrom":[makeQuery(id+"F1.opExtrude","SWEPT_FACE",FACE,{"disambiguationData":[OSD([subQ1,subQ0])]}),makeQuery(id+"F2.opExtrude","SWEPT_FACE",FACE,{"disambiguationData":[OSD([subQ0])]})]})],"blendedInto":[makeQuery(id+"F2.boolean.opBoolean","MERGE",FACE,{"derivedFrom":[makeQuery(id+"F1.opExtrude","SWEPT_FACE",FACE,{"disambiguationData":[OSD([subQ1,subQ0])]}),makeQuery(id+"F2.opExtrude","SWEPT_FACE",FACE,{"disambiguationData":[OSD([subQ0])]})]})]});}
            var Q13;
            {var subQ0=sQuery(id+"F0.wireOp",EDGE,"E0.rect.right");var subQ1=sQuery(id+"F0.wireOp",EDGE,"E0.rect.bottom");var subQ2=sQuery(id+"F0.wireOp",EDGE,"E8.left");Q13=makeQuery(id+"F6.opFillet","BLEND_EDGE",EDGE,{"blendedFrom":[makeQuery(id+"F5.opFillet","BLEND_EDGE",EDGE,{"blendedFrom":[makeQuery(id+"F2.opExtrude","SWEPT_EDGE",EDGE,{"disambiguationData":[OSD([subQ0,sQuery(id+"F0.wireOp",EDGE,"E8.bottom"),subQ2])]}),makeQuery(id+"F1.opExtrude","CAP_FACE",FACE,{"disambiguationData":[OSD([subQ1,sQuery(id+"F0.wireOp",EDGE,"E0.rect.left"),subQ0,sQuery(id+"F0.wireOp",EDGE,"E1.rect.bottom"),sQuery(id+"F0.wireOp",EDGE,"E1.rect.top"),sQuery(id+"F0.wireOp",EDGE,"E1.rect.left"),sQuery(id+"F0.wireOp",EDGE,"E1.rect.right"),sQuery(id+"F0.wireOp",EDGE,"E2"),sQuery(id+"F0.wireOp",EDGE,"E3"),sQuery(id+"F0.wireOp",EDGE,"E4.trimOffspring"),subQ2])],"isStart":false})],"blendedInto":[makeQuery(id+"F1.opExtrude","CAP_FACE",FACE,{"disambiguationData":[OSD([subQ1,sQuery(id+"F0.wireOp",EDGE,"E0.rect.left"),subQ0,sQuery(id+"F0.wireOp",EDGE,"E1.rect.bottom"),sQuery(id+"F0.wireOp",EDGE,"E1.rect.top"),sQuery(id+"F0.wireOp",EDGE,"E1.rect.left"),sQuery(id+"F0.wireOp",EDGE,"E1.rect.right"),sQuery(id+"F0.wireOp",EDGE,"E2"),sQuery(id+"F0.wireOp",EDGE,"E3"),sQuery(id+"F0.wireOp",EDGE,"E4.trimOffspring"),subQ2])],"isStart":false})]}),makeQuery(id+"F4.opFillet","BLEND_FACE",FACE,{"disambiguationData":[OSD([subQ1,subQ0])]})],"blendedInto":[makeQuery(id+"F4.opFillet","BLEND_FACE",FACE,{"disambiguationData":[OSD([subQ1,subQ0])]})]});}
            var Q14;
            {var subQ0=sQuery(id+"F0.wireOp",EDGE,"E8.left");var subQ1=sQuery(id+"F0.wireOp",EDGE,"E0.rect.right");Q14=makeQuery(id+"F6.opFillet","BLEND_EDGE",EDGE,{"blendedFrom":[makeQuery(id+"F5.opFillet","BLEND_EDGE",EDGE,{"blendedFrom":[makeQuery(id+"F2.opExtrude","SWEPT_EDGE",EDGE,{"disambiguationData":[OSD([subQ1,sQuery(id+"F0.wireOp",EDGE,"E8.bottom"),subQ0])]}),makeQuery(id+"F1.opExtrude","CAP_FACE",FACE,{"disambiguationData":[OSD([sQuery(id+"F0.wireOp",EDGE,"E0.rect.bottom"),sQuery(id+"F0.wireOp",EDGE,"E0.rect.left"),subQ1,sQuery(id+"F0.wireOp",EDGE,"E1.rect.bottom"),sQuery(id+"F0.wireOp",EDGE,"E1.rect.top"),sQuery(id+"F0.wireOp",EDGE,"E1.rect.left"),sQuery(id+"F0.wireOp",EDGE,"E1.rect.right"),sQuery(id+"F0.wireOp",EDGE,"E2"),sQuery(id+"F0.wireOp",EDGE,"E3"),sQuery(id+"F0.wireOp",EDGE,"E4.trimOffspring"),subQ0])],"isStart":false})],"blendedInto":[makeQuery(id+"F1.opExtrude","CAP_FACE",FACE,{"disambiguationData":[OSD([sQuery(id+"F0.wireOp",EDGE,"E0.rect.bottom"),sQuery(id+"F0.wireOp",EDGE,"E0.rect.left"),subQ1,sQuery(id+"F0.wireOp",EDGE,"E1.rect.bottom"),sQuery(id+"F0.wireOp",EDGE,"E1.rect.top"),sQuery(id+"F0.wireOp",EDGE,"E1.rect.left"),sQuery(id+"F0.wireOp",EDGE,"E1.rect.right"),sQuery(id+"F0.wireOp",EDGE,"E2"),sQuery(id+"F0.wireOp",EDGE,"E3"),sQuery(id+"F0.wireOp",EDGE,"E4.trimOffspring"),subQ0])],"isStart":false})]}),makeQuery(id+"F2.boolean.opBoolean","MERGE",FACE,{"derivedFrom":[makeQuery(id+"F1.opExtrude","SWEPT_FACE",FACE,{"disambiguationData":[OSD([subQ1,subQ0])]}),makeQuery(id+"F2.opExtrude","SWEPT_FACE",FACE,{"disambiguationData":[OSD([subQ0])]})]})],"blendedInto":[makeQuery(id+"F2.boolean.opBoolean","MERGE",FACE,{"derivedFrom":[makeQuery(id+"F1.opExtrude","SWEPT_FACE",FACE,{"disambiguationData":[OSD([subQ1,subQ0])]}),makeQuery(id+"F2.opExtrude","SWEPT_FACE",FACE,{"disambiguationData":[OSD([subQ0])]})]})]});}
            var Q15;
            Q15=makeQuery(id+"F1.opExtrude","CAP_EDGE",EDGE,{"disambiguationData":[OSD([sQuery(id+"F0.wireOp",EDGE,"E2")])],"isStart":true});
            fillet(context, id + "F7", {"entities" : qUnion([Q0, Q1, Q2, Q3, Q4, Q5, Q6, Q7, Q8, Q9, Q10, Q11, Q12, Q13, Q14, Q15]), "radius" : 0.38 * mm, "tangentPropagation" : true, "allowEdgeOverflow" : false});
        }
        {
            var Q0;
            Q0=makeQuery(id+"F1.opExtrude","CAP_EDGE",EDGE,{"disambiguationData":[OSD([sQuery(id+"F0.wireOp",EDGE,"E1.rect.left")])],"isStart":true});
            var Q1;
            Q1=makeQuery(id+"F1.opExtrude","CAP_EDGE",EDGE,{"disambiguationData":[OSD([sQuery(id+"F0.wireOp",EDGE,"E1.rect.right")])],"isStart":true});
            var Q2;
            Q2=makeQuery(id+"F1.opExtrude","CAP_EDGE",EDGE,{"disambiguationData":[OSD([sQuery(id+"F0.wireOp",EDGE,"E1.rect.top")])],"isStart":true});
            var Q3;
            Q3=makeQuery(id+"F1.opExtrude","CAP_EDGE",EDGE,{"disambiguationData":[OSD([sQuery(id+"F0.wireOp",EDGE,"E1.rect.bottom")])],"isStart":true});
            var Q4;
            Q4=makeQuery(id+"F1.opExtrude","CAP_EDGE",EDGE,{"disambiguationData":[OSD([sQuery(id+"F0.wireOp",EDGE,"E1.rect.bottom")])],"isStart":false});
            var Q5;
            Q5=makeQuery(id+"F1.opExtrude","CAP_EDGE",EDGE,{"disambiguationData":[OSD([sQuery(id+"F0.wireOp",EDGE,"E1.rect.left")])],"isStart":false});
            var Q6;
            Q6=makeQuery(id+"F1.opExtrude","CAP_EDGE",EDGE,{"disambiguationData":[OSD([sQuery(id+"F0.wireOp",EDGE,"E1.rect.top")])],"isStart":false});
            var Q7;
            Q7=makeQuery(id+"F1.opExtrude","CAP_EDGE",EDGE,{"disambiguationData":[OSD([sQuery(id+"F0.wireOp",EDGE,"E1.rect.right")])],"isStart":false});
            fillet(context, id + "F8", {"entities" : qUnion([Q0, Q1, Q2, Q3, Q4, Q5, Q6, Q7]), "radius" : 0.25 * mm, "tangentPropagation" : true, "allowEdgeOverflow" : false});
        }
    });
